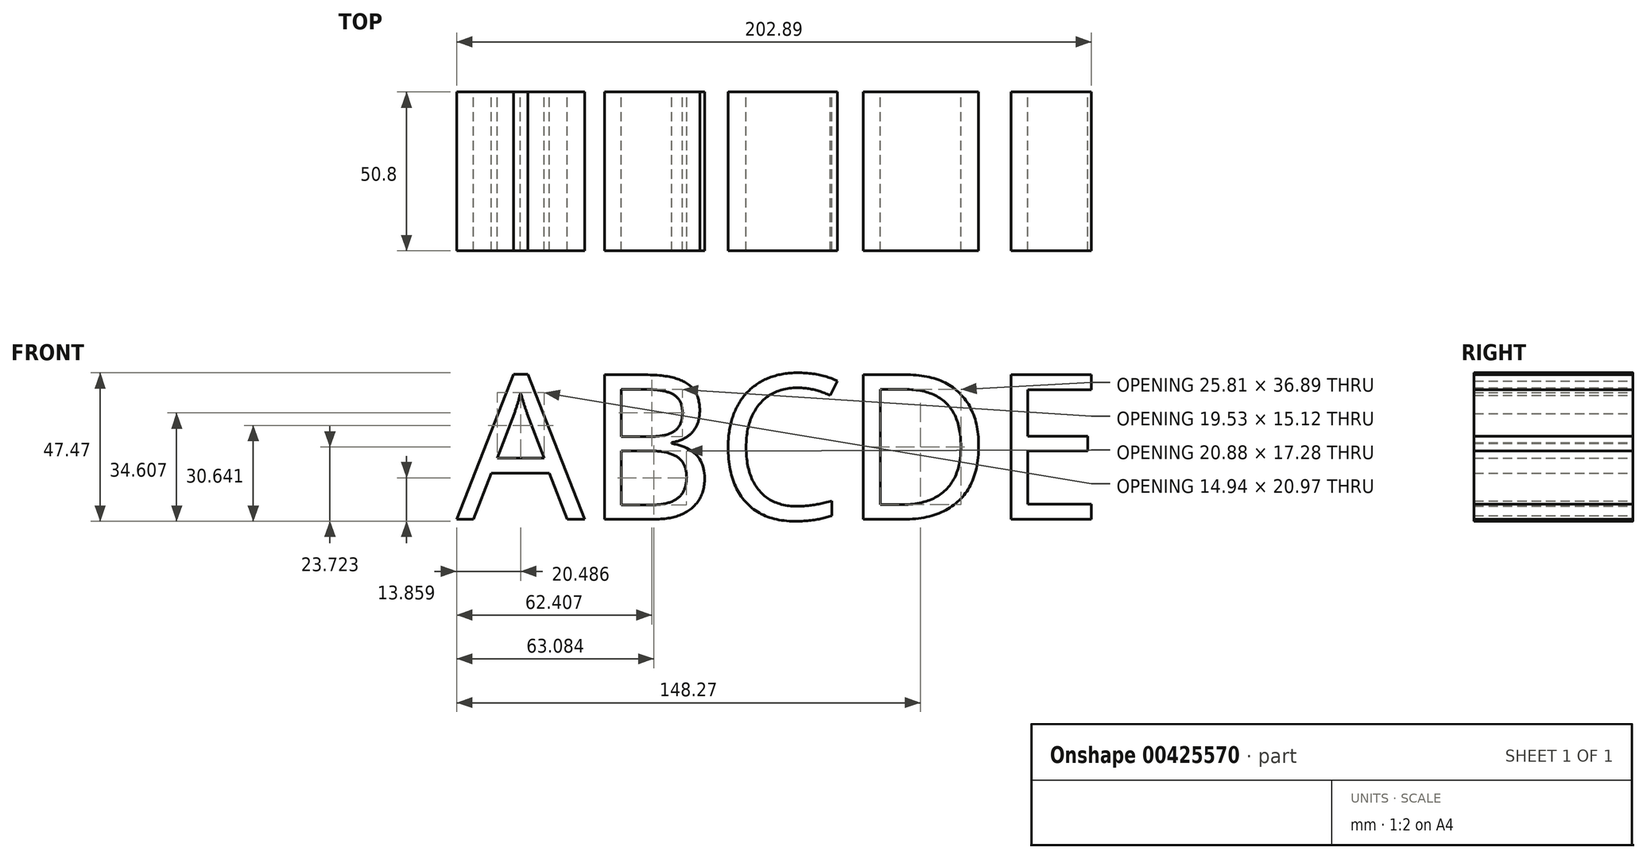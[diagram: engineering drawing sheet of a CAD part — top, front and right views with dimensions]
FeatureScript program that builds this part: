
annotation { "Feature Type Name" : "Feature", "Feature Type Description" : "" }
export const myFeature = defineFeature(function(context is Context, id is Id, definition is map)
    precondition{}
    {
        {
            var Q0;
            Q0=qCreatedBy(makeId("Front.planeOp"),FACE);
            var sketch = newSketch(context, id + "F0", { "sketchPlane" : qUnion([Q0])});
            skText(sketch, "E0", { "text": "ABCDEFG", "fontName": "OpenSans-Regular.ttf"});
            const initialGuessF0  = {"E0": [-0.1298, -0.02708, 1, 0, 0.04657]};
            skSetInitialGuess(sketch, initialGuessF0);
            skSolve(sketch);
        }
        {
            var Q0;
            Q0 = qSketchRegion(id + "F0", true);
            extrude(context, id + "F1", {"entities" : qUnion([Q0]), "depth" : 50.8 * mm});
        }
        {
            var Q0;
            Q0=makeQuery(id+"F1.opExtrude","SWEPT_BODY",BODY,{"disambiguationData":[OSD([sQuery(id+"F0.wireOp",EDGE,"E0.sketch_text.stroke-89"),sQuery(id+"F0.wireOp",EDGE,"E0.sketch_text.stroke-90"),sQuery(id+"F0.wireOp",EDGE,"E0.sketch_text.stroke-91"),sQuery(id+"F0.wireOp",EDGE,"E0.sketch_text.stroke-92"),sQuery(id+"F0.wireOp",EDGE,"E0.sketch_text.stroke-93"),sQuery(id+"F0.wireOp",EDGE,"E0.sketch_text.stroke-94"),sQuery(id+"F0.wireOp",EDGE,"E0.sketch_text.stroke-95"),sQuery(id+"F0.wireOp",EDGE,"E0.sketch_text.stroke-96"),sQuery(id+"F0.wireOp",EDGE,"E0.sketch_text.stroke-97"),sQuery(id+"F0.wireOp",EDGE,"E0.sketch_text.stroke-98"),sQuery(id+"F0.wireOp",EDGE,"E0.sketch_text.stroke-99"),sQuery(id+"F0.wireOp",EDGE,"E0.sketch_text.stroke-100"),sQuery(id+"F0.wireOp",EDGE,"E0.sketch_text.stroke-101"),sQuery(id+"F0.wireOp",EDGE,"E0.sketch_text.stroke-102"),sQuery(id+"F0.wireOp",EDGE,"E0.sketch_text.stroke-103"),sQuery(id+"F0.wireOp",EDGE,"E0.sketch_text.stroke-104"),sQuery(id+"F0.wireOp",EDGE,"E0.sketch_text.stroke-105"),sQuery(id+"F0.wireOp",EDGE,"E0.sketch_text.stroke-106"),sQuery(id+"F0.wireOp",EDGE,"E0.sketch_text.stroke-107"),sQuery(id+"F0.wireOp",EDGE,"E0.sketch_text.stroke-108")])]});
            deleteBodies(context, id + "F2", {"entities" : qUnion([Q0])});
        }
        {
            var Q0;
            Q0=makeQuery(id+"F1.opExtrude","SWEPT_BODY",BODY,{"disambiguationData":[OSD([sQuery(id+"F0.wireOp",EDGE,"E0.sketch_text.stroke-79"),sQuery(id+"F0.wireOp",EDGE,"E0.sketch_text.stroke-80"),sQuery(id+"F0.wireOp",EDGE,"E0.sketch_text.stroke-81"),sQuery(id+"F0.wireOp",EDGE,"E0.sketch_text.stroke-82"),sQuery(id+"F0.wireOp",EDGE,"E0.sketch_text.stroke-83"),sQuery(id+"F0.wireOp",EDGE,"E0.sketch_text.stroke-84"),sQuery(id+"F0.wireOp",EDGE,"E0.sketch_text.stroke-85"),sQuery(id+"F0.wireOp",EDGE,"E0.sketch_text.stroke-86"),sQuery(id+"F0.wireOp",EDGE,"E0.sketch_text.stroke-87"),sQuery(id+"F0.wireOp",EDGE,"E0.sketch_text.stroke-88")])]});
            deleteBodies(context, id + "F3", {"entities" : qUnion([Q0])});
        }
    });
